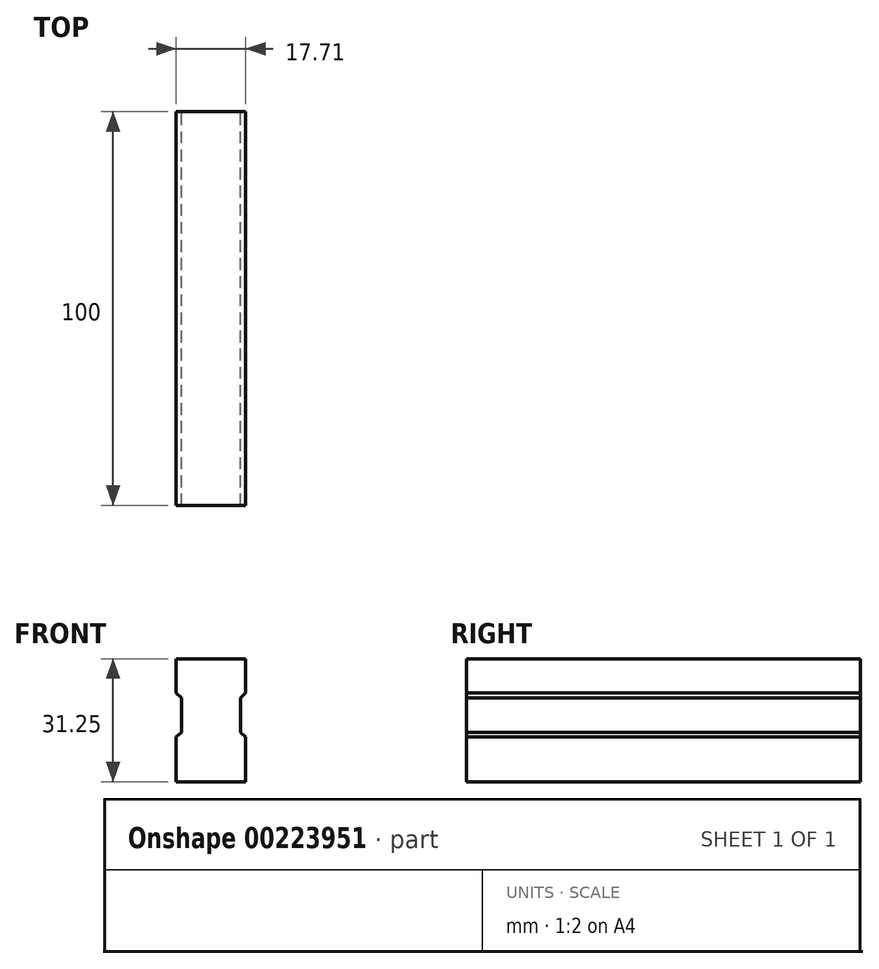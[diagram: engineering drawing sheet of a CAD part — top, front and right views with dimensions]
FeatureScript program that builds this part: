
annotation { "Feature Type Name" : "Feature", "Feature Type Description" : "" }
export const myFeature = defineFeature(function(context is Context, id is Id, definition is map)
    precondition{}
    {
        {
            var Q0;
            Q0=qCreatedBy(makeId("Front.planeOp"),FACE);
            var sketch = newSketch(context, id + "F0", { "sketchPlane" : qUnion([Q0])});
            skLineSegment(sketch, "E0.bottom", {"start": v(0, 0) * mm, "end": v(17.7, 0) * mm, "construction": true});
            skLineSegment(sketch, "E0.top", {"start": v(0, 31.25) * mm, "end": v(17.7, 31.25) * mm, "construction": true});
            skLineSegment(sketch, "E0.left", {"start": v(0, 0) * mm, "end": v(0, 31.25) * mm, "construction": true});
            skLineSegment(sketch, "E0.right", {"start": v(17.7, 0) * mm, "end": v(17.7, 31.25) * mm, "construction": true});
            skLineSegment(sketch, "E1", {"start": v(8.85, 31.25) * mm, "end": v(8.85, 0) * mm, "construction": true});
            skLineSegment(sketch, "E2", {"start": v(8.85, 0) * mm, "end": v(0, 0) * mm});
            skLineSegment(sketch, "E3", {"start": v(0, 11.35) * mm, "end": v(1.35, 12.6) * mm});
            skLineSegment(sketch, "E4", {"start": v(1.35, 12.6) * mm, "end": v(1.35, 21.35) * mm});
            skLineSegment(sketch, "E5", {"start": v(1.35, 21.35) * mm, "end": v(0, 22.6) * mm});
            skLineSegment(sketch, "E6", {"start": v(0, 22.6) * mm, "end": v(0, 31.25) * mm});
            skLineSegment(sketch, "E7", {"start": v(8.85, 31.25) * mm, "end": v(0, 31.25) * mm});
            skLineSegment(sketch, "E8", {"start": v(0, 0) * mm, "end": v(0, 11.35) * mm});
            skLineSegment(sketch, "E9.MirrorCS", {"start": v(16.35, 21.35) * mm, "end": v(17.7, 22.6) * mm});
            skLineSegment(sketch, "E10.MirrorCS", {"start": v(17.7, 11.35) * mm, "end": v(16.35, 12.6) * mm});
            skLineSegment(sketch, "E11.MirrorCS", {"start": v(17.7, 0) * mm, "end": v(17.7, 11.35) * mm});
            skLineSegment(sketch, "E12.MirrorCS", {"start": v(8.85, 31.25) * mm, "end": v(17.7, 31.25) * mm});
            skLineSegment(sketch, "E13.MirrorCS", {"start": v(8.85, 0) * mm, "end": v(17.7, 0) * mm});
            skLineSegment(sketch, "E14.MirrorCS", {"start": v(16.35, 12.6) * mm, "end": v(16.35, 21.35) * mm});
            skLineSegment(sketch, "E15.MirrorCS", {"start": v(17.7, 22.6) * mm, "end": v(17.7, 31.25) * mm});
            skSolve(sketch);
        }
        {
            var Q0;
            Q0=makeQuery(id+"F0.imprint","IMPRINT",FACE,{"disambiguationData":[TD([[makeQuery(id+"F0.imprint","IMPRINT",EDGE,{"derivedFrom":sQuery(id+"F0.wireOp",EDGE,"E2")}),-1.0]])]});
            extrude(context, id + "F1", {"entities" : qUnion([Q0]), "depth" : 100 * mm});
        }
    });
